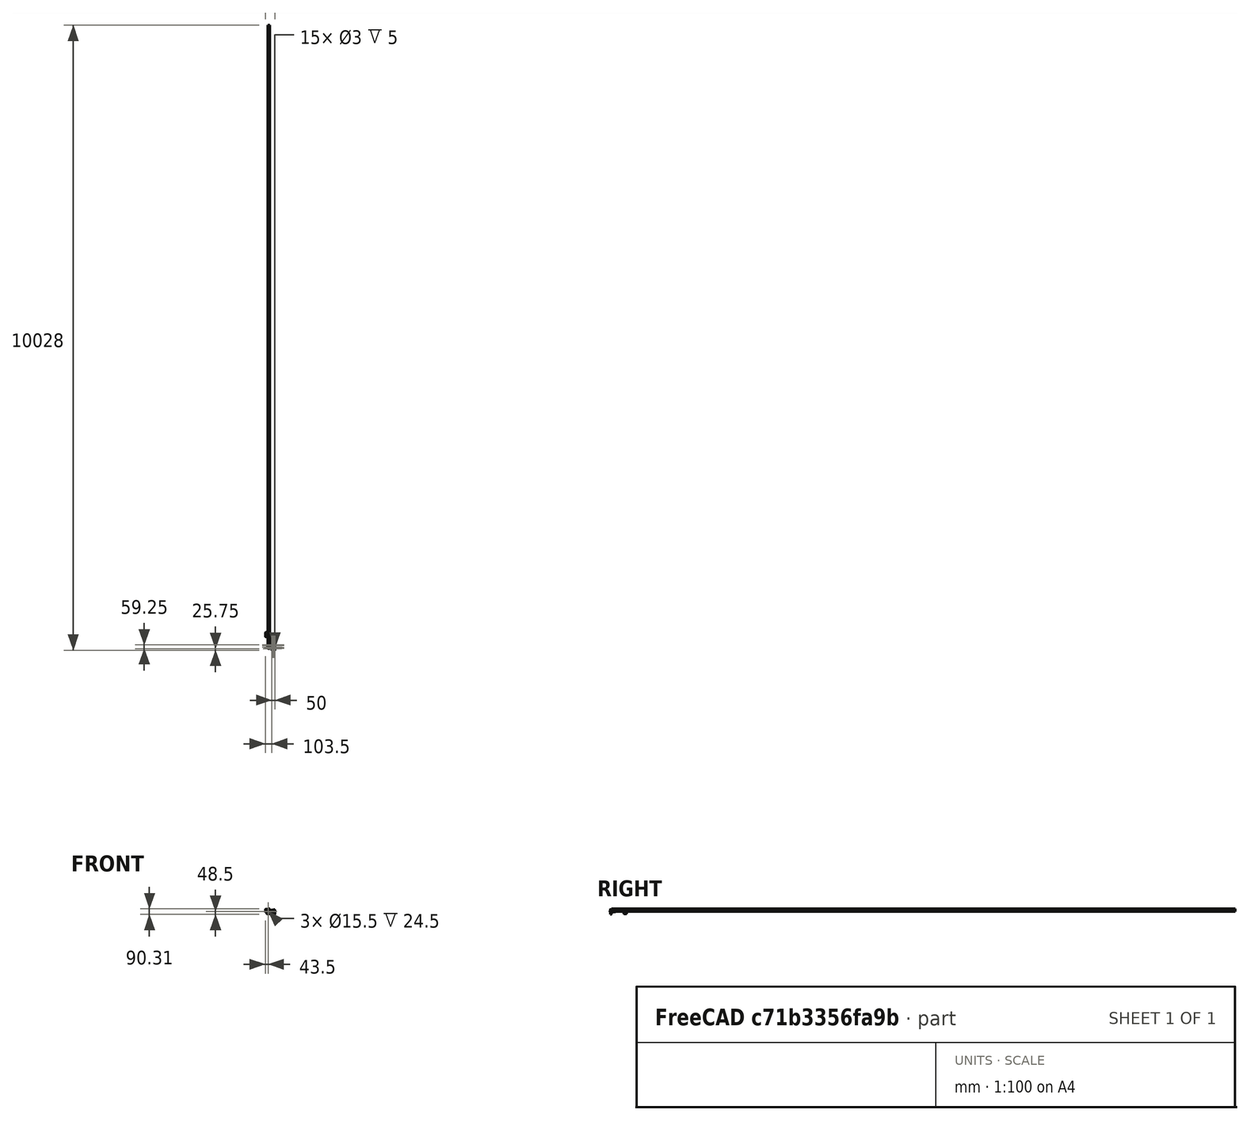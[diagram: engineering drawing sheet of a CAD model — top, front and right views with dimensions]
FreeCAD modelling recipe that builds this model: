
FCSTD DOCUMENT  (FreeCAD 0.15R4671 (Git))
Label: YCarrageBearingCap
License: All rights reserved
LicenseURL: http://en.wikipedia.org/wiki/All_rights_reserved
objects: Part::Feature×17, Mesh::Feature×17, Sketcher::SketchObject×12, PartDesign::Pocket×6, PartDesign::Pad×5, PartDesign::Fillet×1, App::DocumentObjectGroup×1
note: 52 computed .brp shape members not serialized (recipe doc carries the construction recipe); baked Part::Feature solids carry a one-line shape summary decoded from their .brp

FEATURE [Part::Feature] Part__Feature  label="HexagonHotendFanShroud"
  shape: bbox 25.53 x 43.75 x 27.5 mm, 64 faces (baked)
FEATURE [Part::Feature] Part__Feature001  label="XCarrageBottom"
  shape: bbox 57.67 x 92 x 16.5 mm, 140 faces (baked)
FEATURE [Part::Feature] Part__Feature002  label="XCarrageTop"
  shape: bbox 56 x 70.62 x 16.52 mm, 278 faces (baked)
FEATURE [Part::Feature] Part__Feature003  label="LJ18A3"
  Placement = pos=(136,-57,-52) rot=(0,0,1;0rad)
  shape: bbox 17.85 x 17.85 x 79.1 mm, 11 faces (baked)
FEATURE [Mesh::Feature] MicroSwitch
  Placement = pos=(99,-12.5,-5) rot=(0,0,1;1.5708rad)
FEATURE [Mesh::Feature] Fan_25mm_x_10mm
  Placement = pos=(105.5,-31,-25.5) rot=(0,0.707107,0.707107;3.14159rad)
FEATURE [Mesh::Feature] HexHotEnd
  Placement = pos=(104,-57,-34) rot=(0,0,1;0rad)
FEATURE [Mesh::Feature] PNEUMATIC_NIPPLE
  Placement = pos=(111,-66,-3) rot=(0,-1,0;1.5708rad)
FEATURE [Mesh::Feature] HexNutStyle1_M  label="HexNutStyle1_M017"
  Placement = pos=(-16,7.15,12.44) rot=(0.250563,0.935113,0.250563;1.63783rad)
FEATURE [Mesh::Feature] HexNutStyle1_M001  label="HexNutStyle1_M018"
  Placement = pos=(-16,20.15,12.44) rot=(0.250563,0.935113,0.250563;1.63783rad)
FEATURE [Mesh::Feature] HexNutStyle1_M002  label="HexNutStyle1_M019"
  Placement = pos=(22.5,7.15,12.44) rot=(0.250563,0.935113,0.250563;1.63783rad)
FEATURE [Mesh::Feature] HexNutStyle1_M003  label="HexNutStyle1_M020"
  Placement = pos=(22.5,20.15,12.44) rot=(0.250563,0.935113,0.250563;1.63783rad)
FEATURE [Part::Feature] LM8UU_8mm_Linear_Bearing
  Placement = pos=(95,7.5,1.5) rot=(-1,0,0;1.5708rad)
  shape: bbox 24 x 15 x 15 mm, 34 faces (baked)
FEATURE [Part::Feature] LM8UU_8mm_Linear_Bearing001
  Placement = pos=(95,-32.5,1.5) rot=(-1,0,0;1.5708rad)
  shape: bbox 24 x 15 x 15 mm, 34 faces (baked)
FEATURE [Part::Feature] LM8UU_8mm_Linear_Bearing002
  Placement = pos=(123,7.5,1.5) rot=(-1,0,0;1.5708rad)
  shape: bbox 24 x 15 x 15 mm, 34 faces (baked)
FEATURE [Part::Feature] LM8UU_8mm_Linear_Bearing003
  Placement = pos=(123,-32.5,1.5) rot=(-1,0,0;1.5708rad)
  shape: bbox 24 x 15 x 15 mm, 34 faces (baked)
FEATURE [Mesh::Feature] _mmRod_x100mm  label="8mmRod_x100mm001"
  Placement = pos=(45,7.5,1.5) rot=(0,0,1;1.5708rad)
FEATURE [Mesh::Feature] _mmRod_x100mm001  label="8mmRod_x100mm002"
  Placement = pos=(45,-32.5,1.5) rot=(0,0,1;1.5708rad)
FEATURE [Part::Feature] Part__Feature004  label="OB1515_45mm001"
  Placement = pos=(0,191.5,22.5) rot=(1,0,0;1.5708rad)
  shape: bbox 15 x 45 x 15 mm, 158 faces (baked)
FEATURE [Part::Feature] Part__Feature005  label="OB1515_45mm"
  Placement = pos=(7,205,-15) rot=(0,0,1;0.785398rad)
  shape: bbox 21.01 x 21.01 x 45 mm, 158 faces (baked)
FEATURE [Part::Feature] Part__Feature006  label="OB1515_45mm002"
  Placement = pos=(20.5,212,22.5) rot=(0.57735,0.57735,0.57735;2.0944rad)
  shape: bbox 45 x 15 x 15 mm, 158 faces (baked)
FEATURE [Part::Feature] Part__Feature007  label="NEMA17"
  Placement = pos=(36,176,2) rot=(0,0,1;0rad)
  shape: bbox 42.3 x 42.3 x 68 mm, 275 faces (baked)
FEATURE [Part::Feature] Part__Feature008  label="T5_Pulley"
  Placement = pos=(36,176,-4) rot=(0,0,1;0rad)
  shape: bbox 16 x 16 x 14.8 mm, 116 faces (baked)
FEATURE [Mesh::Feature] _mmRod_x100mm002  label="8mmRod_x100mm"
  Placement = pos=(36,47.5,-3.5) rot=(0,0,1;3.14159rad)
FEATURE [Part::Feature] Part__Feature009  label="TopCornerMotor"
  Placement = pos=(0,212,0) rot=(0,0,1;0rad)
  shape: bbox 69.55 x 77 x 28 mm, 82 faces (baked)
FEATURE [Part::Feature] Part__Feature010  label="TopRodHolder"
  Placement = pos=(0,212,2) rot=(0,0,1;0rad)
  shape: bbox 30.16 x 11.33 x 11.99 mm, 58 faces (baked)
FEATURE [Part::Feature] LM8UU_8mm_Linear_Bearing004
  Placement = pos=(36,-9,-3.5) rot=(0,0,1;1.5708rad)
  shape: bbox 15 x 24 x 15 mm, 34 faces (baked)
FEATURE [Mesh::Feature] _x10x4_FlangedBearing  label="5x10x4_FlangedBearing_BOTTOM"
  Placement = pos=(49,-6,16) rot=(-1,0,0;1.5708rad)
FEATURE [Mesh::Feature] _x10x4_FlangedBearing001  label="5x10x4_FlangedBearing_TOP"
  Placement = pos=(49,-6,12) rot=(1,0,0;1.5708rad)
FEATURE [Mesh::Feature] _x10x4_FlangedBearing002  label="5x10x4_FlangedBearing_BOTTOM001"
  Placement = pos=(49,-19,16) rot=(-1,0,0;1.5708rad)
FEATURE [Mesh::Feature] _x10x4_FlangedBearing003  label="5x10x4_FlangedBearing_TOP001"
  Placement = pos=(49,-19,12) rot=(1,0,0;1.5708rad)
FEATURE [Part::Feature] LM8UU_8mm_Linear_Bearing005
  Placement = pos=(36,-40,-3.5) rot=(0,0,1;1.5708rad)
  shape: bbox 15 x 24 x 15 mm, 34 faces (baked)
FEATURE [Sketcher::SketchObject] Sketch
  Placement = pos=(0,0,-14) rot=(0,0,1;0rad)
  sketch-geometry (4):
    g0: LineSegment StartX=25 StartY=17 StartZ=0 EndX=60 EndY=17 EndZ=0
    g1: LineSegment StartX=60 StartY=17 StartZ=0 EndX=60 EndY=-42 EndZ=0
    g2: LineSegment StartX=60 StartY=-42 StartZ=0 EndX=25 EndY=-42 EndZ=0
    g3: LineSegment StartX=25 StartY=-42 StartZ=0 EndX=25 EndY=17 EndZ=0
  constraints (8):
    c: Coincident(g0,g1)
    c: Coincident(g1,g2)
    c: Coincident(g2,g3)
    c: Coincident(g3,g0)
    c: Horizontal(g0)
    c: Horizontal(g2)
    c: Vertical(g1)
    c: Vertical(g3)
FEATURE [PartDesign::Pad] Pad
  Length = 23
  Length2 = 100
  Placement = pos=(0,0,-14) rot=(0,0,1;0rad)
  Sketch = -> Sketch
  Type = 0
FEATURE [Sketcher::SketchObject] Sketch001
  Placement = pos=(0,0,9) rot=(0,0,1;0rad)
  Support = -> Pad [Face6]
  sketch-geometry (16):
    g0: ArcOfCircle CenterX=49 CenterY=-6 CenterZ=0 NormalX=0 NormalY=0 NormalZ=1 Radius=7 StartAngle=0 EndAngle=1.5708
    g1: ArcOfCircle CenterX=49 CenterY=-19 CenterZ=0 NormalX=0 NormalY=0 NormalZ=1 Radius=7 StartAngle=4.71239 EndAngle=6.28248
    g2: LineSegment StartX=56 StartY=-6 StartZ=0 EndX=56 EndY=-7 EndZ=0
    g3: LineSegment StartX=56 StartY=-7 StartZ=0 EndX=59 EndY=-10 EndZ=0
    g4: LineSegment StartX=59 StartY=-10 StartZ=0 EndX=60 EndY=-10 EndZ=0
    g5: LineSegment StartX=60 StartY=-10 StartZ=0 EndX=60 EndY=17 EndZ=0
    g6: LineSegment StartX=60 StartY=17 StartZ=0 EndX=45 EndY=17 EndZ=0
    g7: LineSegment StartX=45 StartY=17 StartZ=0 EndX=45 EndY=1 EndZ=0
    g8: LineSegment StartX=45 StartY=1 StartZ=0 EndX=49 EndY=1 EndZ=0
    g9: LineSegment StartX=49 StartY=-26 StartZ=0 EndX=45 EndY=-26 EndZ=0
    g10: LineSegment StartX=45 StartY=-26 StartZ=0 EndX=45 EndY=-42 EndZ=0
    g11: LineSegment StartX=45 StartY=-42 StartZ=0 EndX=60 EndY=-42 EndZ=0
    g12: LineSegment StartX=60 StartY=-42 StartZ=0 EndX=60 EndY=-15 EndZ=0
    g13: LineSegment StartX=60 StartY=-15 StartZ=0 EndX=59 EndY=-15 EndZ=0
    g14: LineSegment StartX=59 StartY=-15 StartZ=0 EndX=56 EndY=-18 EndZ=0
    g15: LineSegment StartX=56 StartY=-18 StartZ=0 EndX=56 EndY=-19.005 EndZ=0
  constraints (16):
    c: Coincident(g2,g3)
    c: Coincident(g3,g4)
    c: Coincident(g4,g5)
    c: Coincident(g5,g6)
    c: Coincident(g6,g7)
    c: Coincident(g7,g8)
    c: Coincident(g9,g10)
    c: Coincident(g10,g11)
    c: Coincident(g11,g12)
    c: Coincident(g12,g13)
    c: Coincident(g13,g14)
    c: Coincident(g14,g15)
    c: Coincident(g1,g15)
    c: Coincident(g1,g9)
    c: Coincident(g0,g8)
    c: Coincident(g0,g2)
FEATURE [PartDesign::Pad] Pad001
  Length = 10
  Length2 = 100
  Placement = pos=(0,0,-14) rot=(0,0,1;0rad)
  Sketch = -> Sketch001
  Type = 0
FEATURE [Sketcher::SketchObject] Sketch002
  Placement = pos=(0,0,19) rot=(0,0,1;0rad)
  Support = -> Pad001 [Face16]
  sketch-geometry (4):
    g0: LineSegment StartX=45 StartY=17 StartZ=0 EndX=60 EndY=17 EndZ=0
    g1: LineSegment StartX=60 StartY=17 StartZ=0 EndX=60 EndY=-42 EndZ=0
    g2: LineSegment StartX=60 StartY=-42 StartZ=0 EndX=45 EndY=-42 EndZ=0
    g3: LineSegment StartX=45 StartY=-42 StartZ=0 EndX=45 EndY=17 EndZ=0
  constraints (8):
    c: Coincident(g0,g1)
    c: Coincident(g1,g2)
    c: Coincident(g2,g3)
    c: Coincident(g3,g0)
    c: Horizontal(g0)
    c: Horizontal(g2)
    c: Vertical(g1)
    c: Vertical(g3)
FEATURE [PartDesign::Pad] Pad002
  Length = 3
  Length2 = 100
  Placement = pos=(0,0,-14) rot=(0,0,1;0rad)
  Sketch = -> Sketch002
  Type = 0
FEATURE [PartDesign::Fillet] Fillet
  Base = -> Pad002 [Edge32,Edge53]
  Placement = pos=(0,0,-14) rot=(0,0,1;0rad)
  Radius = 2.5
FEATURE [Sketcher::SketchObject] Sketch003
  Placement = pos=(0,-42,-14) rot=(1,0,0;1.5708rad)
  Support = -> Fillet [Face8]
  sketch-geometry (1):
    g0: Circle CenterX=36 CenterY=10.5 CenterZ=0 NormalX=0 NormalY=0 NormalZ=1 Radius=7.75
  constraints (1):
    c: Radius(g0) = 7.75
FEATURE [PartDesign::Pocket] Pocket
  Length = 26.25
  Placement = pos=(0,0,-14) rot=(0,0,1;0rad)
  Sketch = -> Sketch003
  Type = 0
FEATURE [Sketcher::SketchObject] Sketch004
  Placement = pos=(0,17,-14) rot=(0,0.707107,0.707107;3.14159rad)
  Support = -> Pocket [Face4]
  sketch-geometry (1):
    g0: Circle CenterX=-36 CenterY=10.5 CenterZ=0 NormalX=0 NormalY=0 NormalZ=1 Radius=7.75
  constraints (1):
    c: Radius(g0) = 7.75
FEATURE [PartDesign::Pocket] Pocket001
  Length = 26.25
  Placement = pos=(0,0,-14) rot=(0,0,1;0rad)
  Sketch = -> Sketch004
  Type = 0
FEATURE [Sketcher::SketchObject] Sketch005
  Placement = pos=(0,-42,-14) rot=(1,0,0;1.5708rad)
  Support = -> Pocket001 [Face8]
  sketch-geometry (1):
    g0: Circle CenterX=36 CenterY=10.5 CenterZ=0 NormalX=0 NormalY=0 NormalZ=1 Radius=8.5
FEATURE [PartDesign::Pad] Pad003
  Length = 1.75
  Length2 = 100
  Placement = pos=(0,0,-14) rot=(0,0,1;0rad)
  Reversed = true
  Sketch = -> Sketch005
  Type = 0
FEATURE [Sketcher::SketchObject] Sketch006
  Placement = pos=(0,17,-14) rot=(0,0.707107,0.707107;3.14159rad)
  Support = -> Pad003 [Face4]
  sketch-geometry (1):
    g0: Circle CenterX=-36 CenterY=10.5 CenterZ=0 NormalX=0 NormalY=0 NormalZ=1 Radius=9
FEATURE [PartDesign::Pad] Pad004
  Length = 1.75
  Length2 = 100
  Placement = pos=(0,0,-14) rot=(0,0,1;0rad)
  Reversed = true
  Sketch = -> Sketch006
  Type = 0
FEATURE [App::DocumentObjectGroup] Group  label="OtherParts"
  Group = -> [Part__Feature,Part__Feature001,Part__Feature003,Part__Feature002,MicroSwitch,Fan_25mm_x_10mm,HexHotEnd,PNEUMATIC_NIPPLE,HexNutStyle1_M,HexNutStyle1_M001,HexNutStyle1_M002,HexNutStyle1_M003,LM8UU_8mm_Linear_Bearing,LM8UU_8mm_Linear_Bearing001,LM8UU_8mm_Linear_Bearing002,LM8UU_8mm_Linear_Bearing003]
FEATURE [Sketcher::SketchObject] Sketch007
  Placement = pos=(60,0,-14) rot=(0.57735,0.57735,0.57735;2.0944rad)
  Support = -> Pad004 [Face13]
  sketch-geometry (2):
    g0: Circle CenterX=-32.5 CenterY=15.5 CenterZ=0 NormalX=0 NormalY=0 NormalZ=1 Radius=4.3
    g1: Circle CenterX=7.5 CenterY=15.5 CenterZ=0 NormalX=0 NormalY=0 NormalZ=1 Radius=4.3
  constraints (2):
    c: Radius(g0) = 4.3
    c: Radius(g1) = 4.3
FEATURE [PartDesign::Pocket] Pocket002
  Length = 15
  Placement = pos=(0,0,-14) rot=(0,0,1;0rad)
  Sketch = -> Sketch007
  Type = 0
FEATURE [Sketcher::SketchObject] Sketch008
  Placement = pos=(0,0,22) rot=(0,0,1;0rad)
  Support = -> Pocket002 [Face20]
  sketch-geometry (10):
    g0: LineSegment StartX=44 StartY=19 StartZ=0 EndX=44 EndY=6 EndZ=0
    g1: LineSegment StartX=44 StartY=6 StartZ=0 EndX=45 EndY=6 EndZ=0
    g2: LineSegment StartX=45 StartY=6 StartZ=0 EndX=58 EndY=17 EndZ=0
    g3: LineSegment StartX=58 StartY=17 StartZ=0 EndX=58 EndY=19 EndZ=0
    g4: LineSegment StartX=58 StartY=19 StartZ=0 EndX=44 EndY=19 EndZ=0
    g5: LineSegment StartX=43 StartY=-31 StartZ=0 EndX=45 EndY=-31 EndZ=0
    g6: LineSegment StartX=45 StartY=-31 StartZ=0 EndX=58 EndY=-42 EndZ=0
    g7: LineSegment StartX=58 StartY=-42 StartZ=0 EndX=58 EndY=-44 EndZ=0
    g8: LineSegment StartX=58 StartY=-44 StartZ=0 EndX=43 EndY=-44 EndZ=0
    g9: LineSegment StartX=43 StartY=-44 StartZ=0 EndX=43 EndY=-31 EndZ=0
  constraints (10):
    c: Coincident(g0,g1)
    c: Coincident(g1,g2)
    c: Coincident(g2,g3)
    c: Coincident(g3,g4)
    c: Coincident(g4,g0)
    c: Coincident(g5,g6)
    c: Coincident(g6,g7)
    c: Coincident(g7,g8)
    c: Coincident(g8,g9)
    c: Coincident(g9,g5)
FEATURE [PartDesign::Pocket] Pocket003
  Length = 13
  Placement = pos=(0,0,-14) rot=(0,0,1;0rad)
  Sketch = -> Sketch008
  Type = 0
FEATURE [Sketcher::SketchObject] Sketch009
  Placement = pos=(0,-42,-14) rot=(1,0,0;1.5708rad)
  Support = -> Pocket003 [Face16]
  sketch-geometry (4):
    g0: LineSegment StartX=63.6143 StartY=38.3051 StartZ=0 EndX=36 EndY=38.3051 EndZ=0
    g1: LineSegment StartX=36 StartY=38.3051 StartZ=0 EndX=36 EndY=-3.28694 EndZ=0
    g2: LineSegment StartX=36 StartY=-3.28694 StartZ=0 EndX=63.6143 EndY=-3.28694 EndZ=0
    g3: LineSegment StartX=63.6143 StartY=-3.28694 StartZ=0 EndX=63.6143 EndY=38.3051 EndZ=0
  constraints (8):
    c: Coincident(g0,g1)
    c: Coincident(g1,g2)
    c: Coincident(g2,g3)
    c: Coincident(g3,g0)
    c: Horizontal(g0)
    c: Horizontal(g2)
    c: Vertical(g1)
    c: Vertical(g3)
FEATURE [PartDesign::Pocket] Pocket004
  Length = 5
  Placement = pos=(0,0,-14) rot=(0,0,1;0rad)
  Sketch = -> Sketch009
  Type = 1
FEATURE [Sketcher::SketchObject] Sketch010
  Placement = pos=(0,-42,-14) rot=(1,0,0;1.5708rad)
  Support = -> Pocket004 [Face6]
  sketch-geometry (1):
    g0: Circle CenterX=36 CenterY=10.5 CenterZ=0 NormalX=0 NormalY=0 NormalZ=1 Radius=6
  constraints (1):
    c: Radius(g0) = 6
FEATURE [PartDesign::Pocket] Pocket005
  Length = 5
  Placement = pos=(0,0,-14) rot=(0,0,1;0rad)
  Sketch = -> Sketch010
  Type = 1
FEATURE [Sketcher::SketchObject] Sketch011
  Placement = pos=(25,0,-14) rot=(0.57735,-0.57735,-0.57735;2.0944rad)
  Support = -> Pocket005 [Face2]
  sketch-geometry (4):
    g0: Circle CenterX=28.5 CenterY=-1 CenterZ=0 NormalX=0 NormalY=0 NormalZ=1 Radius=3.3
    g1: Circle CenterX=28.5 CenterY=21.5 CenterZ=0 NormalX=0 NormalY=0 NormalZ=1 Radius=3.3
    g2: Circle CenterX=-3.5 CenterY=-1 CenterZ=0 NormalX=0 NormalY=0 NormalZ=1 Radius=3.3
    g3: Circle CenterX=-3.5 CenterY=20.8616 CenterZ=0 NormalX=0 NormalY=0 NormalZ=1 Radius=3.3
  constraints (9):
    c: Radius(g3) = 3.3
    c: Equal(g3,g1)
    c: Equal(g3,g2)
    c: Equal(g3,g0)
    c: DistanceX(g2,g0) = 32
    c: DistanceX(g2) = -3.5
    c: DistanceY(g2) = -1
    c: DistanceX(g3,g1) = 32
    c: DistanceX(g3,g2) = 0
FEATURE [Mesh::Feature] HexNutStyle1_M004  label="HexNutStyle1_M3"
  Placement = pos=(-90,-2,4.5) rot=(0.250563,0.935113,0.250563;1.63783rad)
FEATURE [Mesh::Feature] HexNutStyle1_M005  label="HexNutStyle1_M021"
  Placement = pos=(-90,-2,4.5) rot=(0.250563,0.935113,0.250563;1.63783rad)
